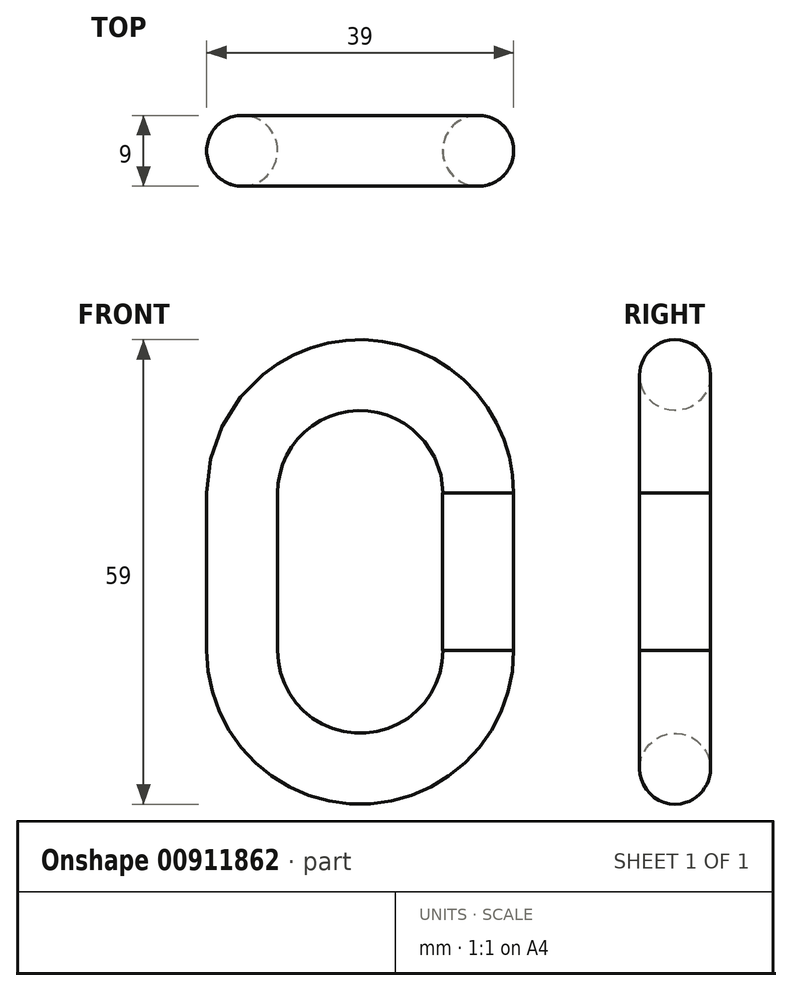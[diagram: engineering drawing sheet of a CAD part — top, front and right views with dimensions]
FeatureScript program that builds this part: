
annotation { "Feature Type Name" : "Feature", "Feature Type Description" : "" }
export const myFeature = defineFeature(function(context is Context, id is Id, definition is map)
    precondition{}
    {
        {
            var Q0;
            Q0=qCreatedBy(makeId("Top.planeOp"),FACE);
            var sketch = newSketch(context, id + "F0", { "sketchPlane" : qUnion([Q0])});
            skCircle(sketch, "E0", {"center": v(0, 0) * mm, "radius": 4.5 * mm});
            skLineSegment(sketch, "E1", {"start": v(15, 13.84) * mm, "end": v(15, -17.25) * mm});
            skSolve(sketch);
        }
        {
            var Q0;
            Q0=makeQuery(id+"F0.imprint","IMPRINT",FACE,{"disambiguationData":[TD([[makeQuery(id+"F0.imprint","IMPRINT",EDGE,{"derivedFrom":sQuery(id+"F0.wireOp",EDGE,"E0")}),1.0]])]});
            var Q1;
            Q1=sQuery(id+"F0.wireOp",EDGE,"E1");
            revolve(context, id + "F1", {"surfaceOperationType" : NewSurfaceOperationType.NEW, "entities" : qUnion([Q0]), "axis" : qUnion([Q1]), "revolveType" : RevolveType.ONE_DIRECTION, "angle" : 180 * degree});
        }
        {
            var Q0;
            Q0=makeQuery(id+"F1.opRevolve","CAP_FACE",FACE,{"disambiguationData":[OSD([sQuery(id+"F0.wireOp",EDGE,"E0")])],"isStart":true});
            var sketch = newSketch(context, id + "F2", { "sketchPlane" : qUnion([Q0])});
            skCircle(sketch, "E2", {"center": v(0, 0) * mm, "radius": 4.5 * mm});
            skCircle(sketch, "E3", {"center": v(29.97, 0) * mm, "radius": 4.5 * mm});
            skSolve(sketch);
        }
        {
            var Q0;
            Q0=makeQuery(id+"F2.imprint","IMPRINT",FACE,{"disambiguationData":[TD([[makeQuery(id+"F2.imprint","IMPRINT",EDGE,{"derivedFrom":sQuery(id+"F2.wireOp",EDGE,"E3")}),1.0]])]});
            var Q1;
            Q1=makeQuery(id+"F2.imprint","IMPRINT",FACE,{"disambiguationData":[TD([[makeQuery(id+"F2.imprint","IMPRINT",EDGE,{"derivedFrom":sQuery(id+"F2.wireOp",EDGE,"E2")}),1.0]])]});
            extrude(context, id + "F3", {"entities" : qUnion([Q0, Q1]), "operationType" : NewBodyOperationType.ADD, "depth" : 20 * mm, "offsetDistance" : 25 * mm});
        }
        {
            var Q0;
            Q0=makeQuery(id+"F3.opExtrude","CAP_FACE",FACE,{"disambiguationData":[OSD([sQuery(id+"F2.wireOp",EDGE,"E2")])],"isStart":false});
            var sketch = newSketch(context, id + "F4", { "sketchPlane" : qUnion([Q0])});
            skLineSegment(sketch, "E4", {"start": v(15, 19.17) * mm, "end": v(15, -20.31) * mm});
            skSolve(sketch);
        }
        {
            var Q0;
            Q0=makeQuery(id+"F4.imprint","IMPRINT",FACE,{"disambiguationData":[TD([[makeQuery(id+"F4.imprint","IMPRINT",EDGE,{"derivedFrom":makeQuery(id+"F3.opExtrude","CAP_EDGE",EDGE,{"disambiguationData":[OSD([sQuery(id+"F2.wireOp",EDGE,"E2")])],"isStart":false})}),1.0]])]});
            var Q1;
            Q1=sQuery(id+"F4.wireOp",EDGE,"E4");
            revolve(context, id + "F5", {"operationType" : NewBodyOperationType.ADD, "surfaceOperationType" : NewSurfaceOperationType.NEW, "entities" : qUnion([Q0]), "axis" : qUnion([Q1]), "revolveType" : RevolveType.ONE_DIRECTION, "oppositeDirection" : true, "angle" : 180 * degree});
        }
    });
